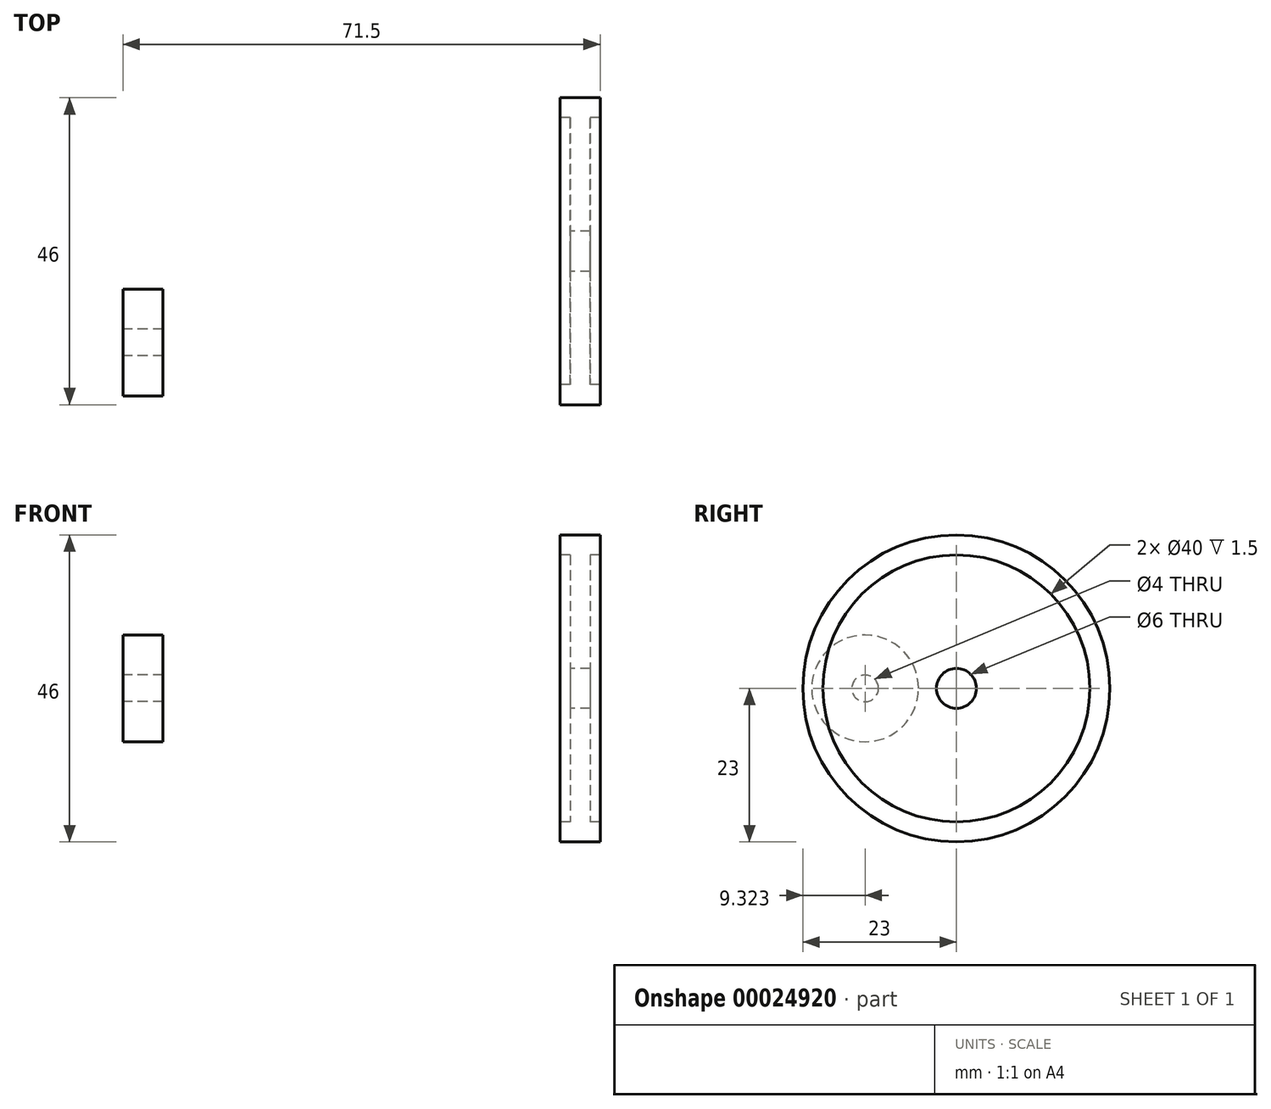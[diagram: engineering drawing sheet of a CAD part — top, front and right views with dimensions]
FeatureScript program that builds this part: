
annotation { "Feature Type Name" : "Feature", "Feature Type Description" : "" }
export const myFeature = defineFeature(function(context is Context, id is Id, definition is map)
    precondition{}
    {
        {
            var Q0;
            Q0=qCreatedBy(makeId("Top.planeOp"),FACE);
            var sketch = newSketch(context, id + "F0", { "sketchPlane" : qUnion([Q0])});
            skLineSegment(sketch, "E0.bottom", {"start": v(30.25, 25.91) * mm, "end": v(33.25, 25.91) * mm});
            skLineSegment(sketch, "E0.left", {"start": v(30.25, 25.91) * mm, "end": v(30.25, 42.91) * mm});
            skLineSegment(sketch, "E0.right", {"start": v(33.25, 25.91) * mm, "end": v(33.25, 42.91) * mm});
            skPoint(sketch, "E1", {"position": v(31.75, 42.91) * mm});
            skLineSegment(sketch, "E2.bottom", {"start": v(28.75, 45.91) * mm, "end": v(34.75, 45.91) * mm});
            skLineSegment(sketch, "E2.top", {"start": v(28.75, 42.91) * mm, "end": v(30.25, 42.91) * mm});
            skLineSegment(sketch, "E2.left", {"start": v(28.75, 45.91) * mm, "end": v(28.75, 42.91) * mm});
            skLineSegment(sketch, "E2.right", {"start": v(34.75, 45.91) * mm, "end": v(34.75, 42.91) * mm});
            skLineSegment(sketch, "E3", {"start": v(1.97, 22.91) * mm, "end": v(65.37, 22.91) * mm, "construction": true});
            skLineSegment(sketch, "E4.trimOffspring", {"start": v(33.25, 42.91) * mm, "end": v(34.75, 42.91) * mm});
            skSolve(sketch);
        }
        {
            var Q0;
            Q0 = qSketchRegion(id + "F0", true);
            var Q1;
            Q1=sQuery(id+"F0.wireOp",EDGE,"E3");
            revolve(context, id + "F1", {"entities" : qUnion([Q0]), "axis" : qUnion([Q1]), "revolveType" : RevolveType.FULL});
        }
        {
            var Q0;
            Q0=qCreatedBy(makeId("Top.planeOp"),FACE);
            var sketch = newSketch(context, id + "F2", { "sketchPlane" : qUnion([Q0])});
            skLineSegment(sketch, "E5", {"start": v(-47.45, 9.23) * mm, "end": v(-22.23, 9.23) * mm, "construction": true});
            skLineSegment(sketch, "E6.bottom", {"start": v(-36.75, 11.23) * mm, "end": v(-30.75, 11.23) * mm});
            skLineSegment(sketch, "E6.top", {"start": v(-36.75, 17.23) * mm, "end": v(-30.75, 17.23) * mm});
            skLineSegment(sketch, "E6.left", {"start": v(-36.75, 11.23) * mm, "end": v(-36.75, 17.23) * mm});
            skLineSegment(sketch, "E6.right", {"start": v(-30.75, 11.23) * mm, "end": v(-30.75, 17.23) * mm});
            skSolve(sketch);
        }
        {
            var Q0;
            Q0 = qSketchRegion(id + "F2", true);
            var Q1;
            Q1=sQuery(id+"F2.wireOp",EDGE,"E5");
            revolve(context, id + "F3", {"entities" : qUnion([Q0]), "axis" : qUnion([Q1]), "revolveType" : RevolveType.FULL});
        }
    });
